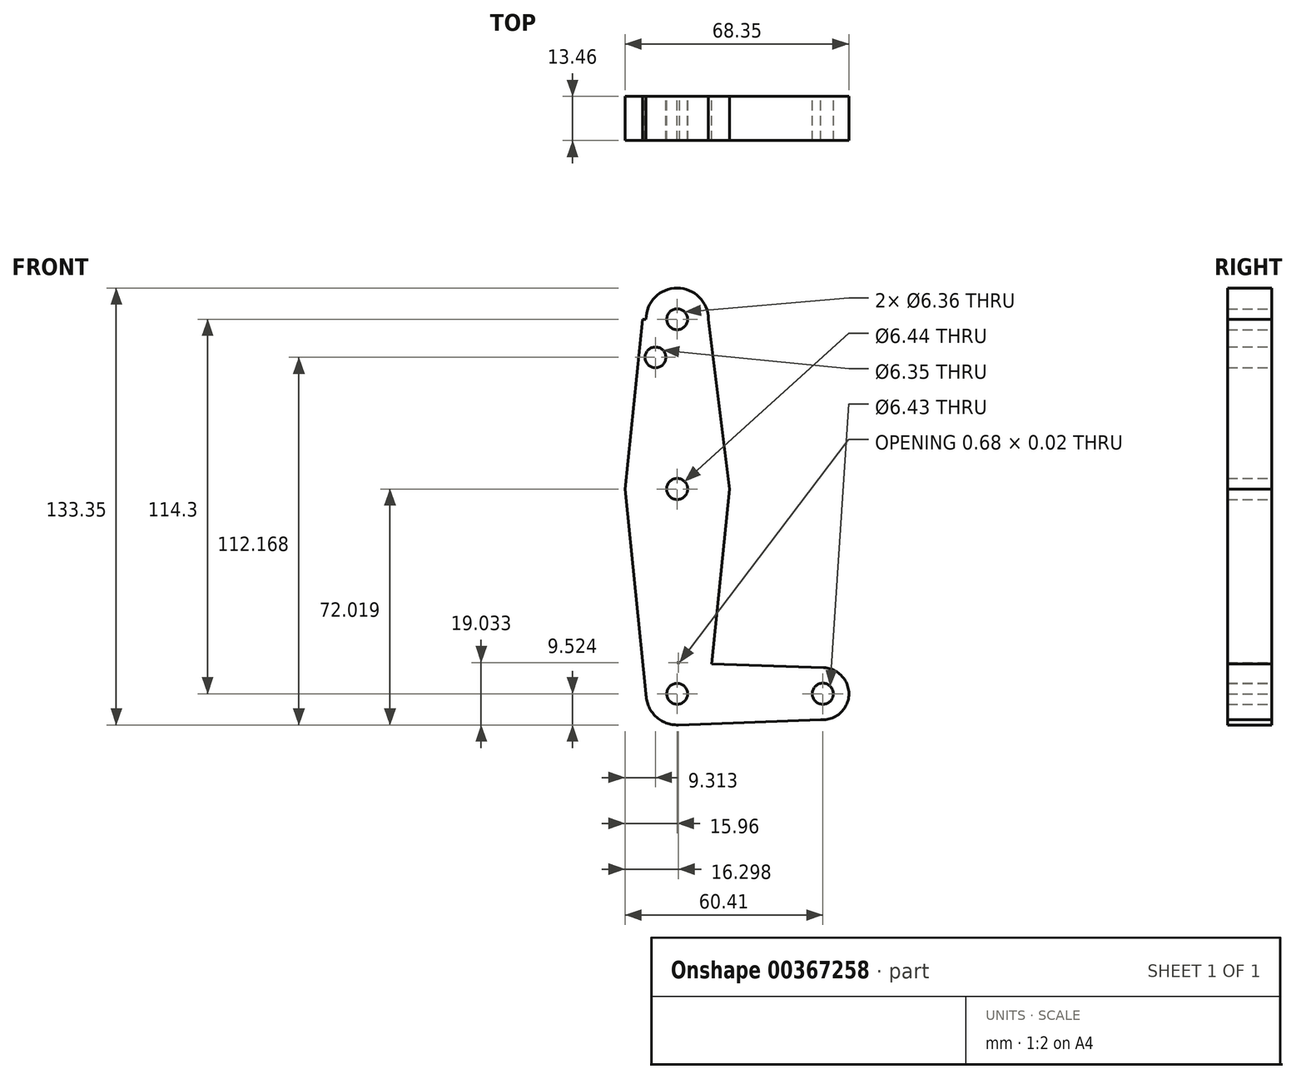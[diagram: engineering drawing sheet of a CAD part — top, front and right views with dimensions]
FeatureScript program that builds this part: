
annotation { "Feature Type Name" : "Feature", "Feature Type Description" : "" }
export const myFeature = defineFeature(function(context is Context, id is Id, definition is map)
    precondition{}
    {
        {
            var Q0;
            Q0=qCreatedBy(makeId("Front.planeOp"),FACE);
            var sketch = newSketch(context, id + "F0", { "sketchPlane" : qUnion([Q0])});
            skLineSegment(sketch, "E0", {"start": v(0, -46.67) * mm, "end": v(0, 67.63) * mm});
            skCircle(sketch, "E1", {"center": v(0, 67.63) * mm, "radius": 9.53 * mm});
            skCircle(sketch, "E2", {"center": v(0, 67.63) * mm, "radius": 3.18 * mm});
            skCircle(sketch, "E3", {"center": v(0, 15.83) * mm, "radius": 15.88 * mm});
            skCircle(sketch, "E4", {"center": v(0, 15.83) * mm, "radius": 3.22 * mm});
            skCircle(sketch, "E5", {"center": v(0, -46.67) * mm, "radius": 9.52 * mm});
            skCircle(sketch, "E6", {"center": v(0, -46.67) * mm, "radius": 3.18 * mm});
            skCircle(sketch, "E7", {"center": v(44.45, -46.67) * mm, "radius": 7.94 * mm});
            skCircle(sketch, "E8", {"center": v(44.45, -46.67) * mm, "radius": 3.21 * mm});
            skLineSegment(sketch, "E9", {"start": v(-9.52, -46.67) * mm, "end": v(-15.96, 15.83) * mm});
            skLineSegment(sketch, "E10", {"start": v(-15.96, 15.83) * mm, "end": v(-10.62, 67.63) * mm});
            skLineSegment(sketch, "E11", {"start": v(-10.62, 67.63) * mm, "end": v(-9.53, 67.63) * mm});
            skLineSegment(sketch, "E12", {"start": v(9.53, 67.63) * mm, "end": v(16, 15.83) * mm});
            skLineSegment(sketch, "E13", {"start": v(16, 15.83) * mm, "end": v(9.57, -46.67) * mm});
            skLineSegment(sketch, "E14", {"start": v(9.57, -46.67) * mm, "end": v(9.52, -46.62) * mm});
            skLineSegment(sketch, "E15", {"start": v(0, -37.14) * mm, "end": v(44.73, -38.73) * mm});
            skLineSegment(sketch, "E16", {"start": v(43.74, -54.57) * mm, "end": v(0, -56.2) * mm});
            skCircle(sketch, "E17", {"center": v(-6.65, 55.98) * mm, "radius": 3.18 * mm});
            skSolve(sketch);
        }
        {
            var Q0;
            Q0 = qSketchRegion(id + "F0", true);
            extrude(context, id + "F1", {"entities" : qUnion([Q0]), "depth" : 13.46 * mm});
        }
    });
